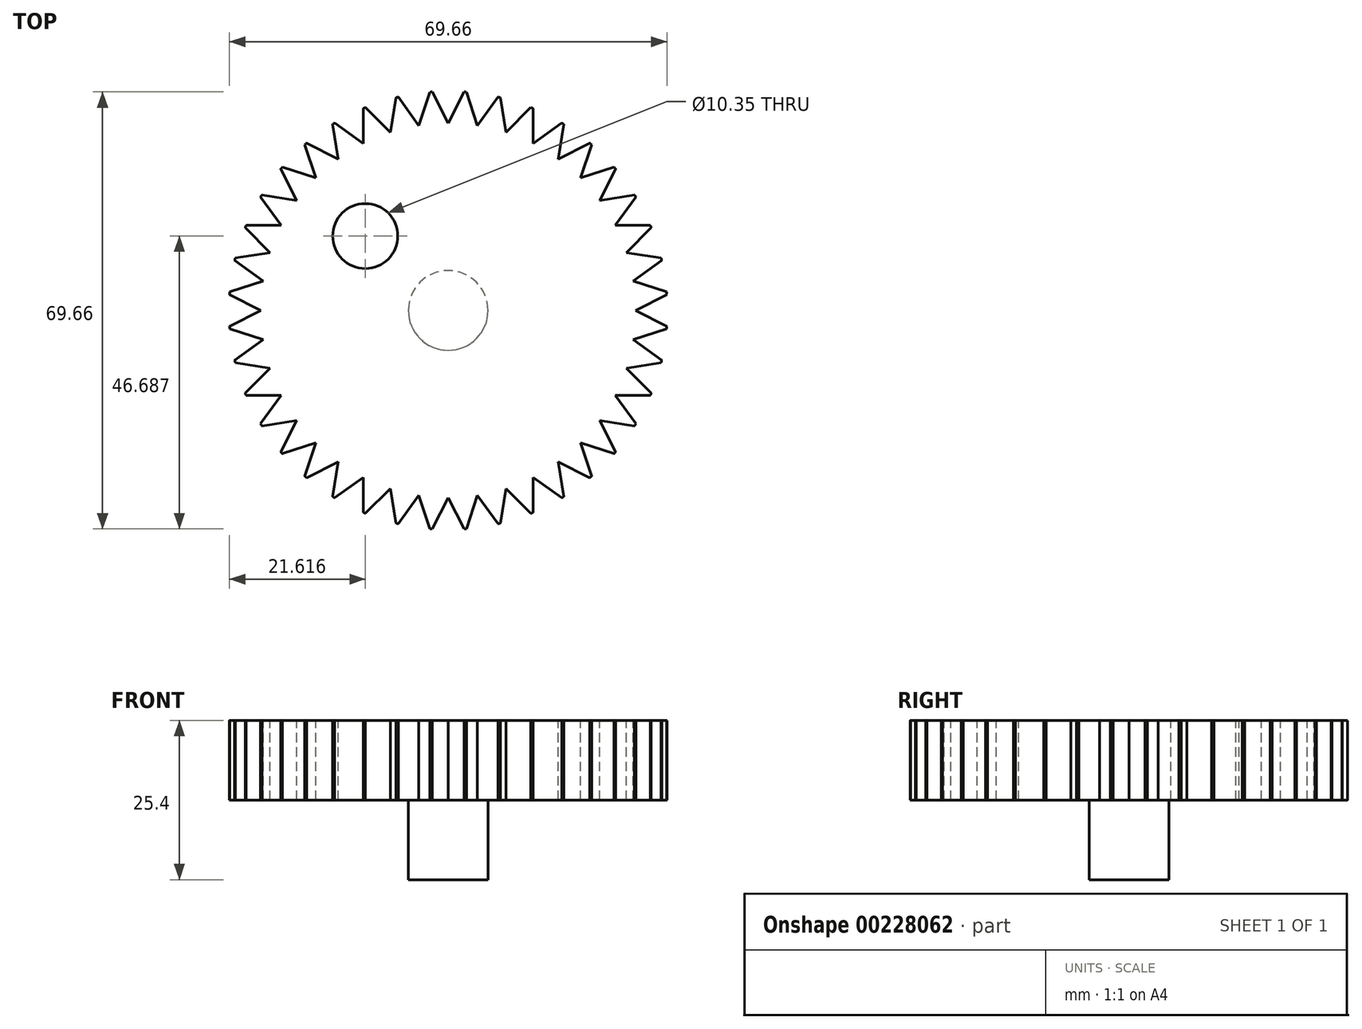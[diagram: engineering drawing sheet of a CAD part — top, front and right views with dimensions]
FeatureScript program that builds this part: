
annotation { "Feature Type Name" : "Feature", "Feature Type Description" : "" }
export const myFeature = defineFeature(function(context is Context, id is Id, definition is map)
    precondition{}
    {
        {
            var Q0;
            Q0=qCreatedBy(makeId("Top.planeOp"),FACE);
            var sketch = newSketch(context, id + "F0", { "sketchPlane" : qUnion([Q0])});
            skCircle(sketch, "E0", {"center": v(0, 0) * mm, "radius": 19.05 * mm});
            skSolve(sketch);
        }
        {
            var Q0;
            Q0=qSketchRegion(id+"F0",true);
            extrude(context, id + "F1", {"entities" : qUnion([Q0]), "depth" : 6.35 * mm, "offsetDistance" : 25.4 * mm});
        }
        {
            var Q0;
            Q0=makeQuery(id+"F1.opExtrude","CAP_FACE",FACE,{"disambiguationData":[OSD([sQuery(id+"F0.wireOp",EDGE,"E0")])],"isStart":false});
            var sketch = newSketch(context, id + "F2", { "sketchPlane" : qUnion([Q0])});
            skCircle(sketch, "E1", {"center": v(0, 0) * mm, "radius": 6.35 * mm});
            skSolve(sketch);
        }
        {
            var Q0;
            Q0=qSketchRegion(id+"F2",true);
            extrude(context, id + "F3", {"entities" : qUnion([Q0]), "operationType" : NewBodyOperationType.ADD, "depth" : 31.75 * mm, "offsetDistance" : 25.4 * mm});
        }
        {
            var Q0;
            Q0=makeQuery(id+"F3.opExtrude","CAP_FACE",FACE,{"disambiguationData":[OSD([sQuery(id+"F2.wireOp",EDGE,"E1")])],"isStart":false});
            var sketch = newSketch(context, id + "F4", { "sketchPlane" : qUnion([Q0])});
            skCircle(sketch, "E2", {"center": v(0, 0) * mm, "radius": 34.93 * mm});
            skSolve(sketch);
        }
        {
            var Q0;
            Q0=qSketchRegion(id+"F4",true);
            extrude(context, id + "F5", {"entities" : qUnion([Q0]), "operationType" : NewBodyOperationType.ADD, "depth" : 12.7 * mm, "offsetDistance" : 25.4 * mm});
        }
        {
            var Q0;
            Q0=makeQuery(id+"F1.opExtrude","CAP_FACE",FACE,{"disambiguationData":[OSD([sQuery(id+"F0.wireOp",EDGE,"E0")])],"isStart":true});
            var sketch = newSketch(context, id + "F6", { "sketchPlane" : qUnion([Q0])});
            skLineSegment(sketch, "E3", {"start": v(0, 16.51) * mm, "end": v(2.54, 18.88) * mm});
            skLineSegment(sketch, "E4", {"start": v(0, 16.51) * mm, "end": v(0, 19.05) * mm, "construction": true});
            skLineSegment(sketch, "E5", {"start": v(0, 16.51) * mm, "end": v(-2.54, 18.88) * mm});
            skArc(sketch, "E6", {"start": v(2.54, 18.88) * mm, "mid": v(0, 19.05) * mm, "end": v(-2.54, 18.88) * mm});
            skLineSegment(sketch, "E7.1.0", {"start": v(-5.1, 15.7) * mm, "end": v(-5.89, 18.12) * mm, "construction": true});
            skLineSegment(sketch, "E7.1.1", {"start": v(-5.1, 15.7) * mm, "end": v(-8.25, 17.17) * mm});
            skArc(sketch, "E7.1.2", {"start": v(-3.42, 18.74) * mm, "mid": v(-5.89, 18.12) * mm, "end": v(-8.25, 17.17) * mm});
            skLineSegment(sketch, "E7.1.3", {"start": v(-5.1, 15.7) * mm, "end": v(-3.42, 18.74) * mm});
            skLineSegment(sketch, "E7.2.0", {"start": v(-9.7, 13.36) * mm, "end": v(-11.2, 15.41) * mm, "construction": true});
            skLineSegment(sketch, "E7.2.1", {"start": v(-9.7, 13.36) * mm, "end": v(-13.15, 13.78) * mm});
            skArc(sketch, "E7.2.2", {"start": v(-9.04, 16.77) * mm, "mid": v(-11.2, 15.41) * mm, "end": v(-13.15, 13.78) * mm});
            skLineSegment(sketch, "E7.2.3", {"start": v(-9.7, 13.36) * mm, "end": v(-9.04, 16.77) * mm});
            skLineSegment(sketch, "E7.3.0", {"start": v(-13.36, 9.7) * mm, "end": v(-15.41, 11.2) * mm, "construction": true});
            skLineSegment(sketch, "E7.3.1", {"start": v(-13.36, 9.7) * mm, "end": v(-16.77, 9.04) * mm});
            skArc(sketch, "E7.3.2", {"start": v(-13.78, 13.15) * mm, "mid": v(-15.41, 11.2) * mm, "end": v(-16.77, 9.04) * mm});
            skLineSegment(sketch, "E7.3.3", {"start": v(-13.36, 9.7) * mm, "end": v(-13.78, 13.15) * mm});
            skLineSegment(sketch, "E7.4.0", {"start": v(-15.7, 5.1) * mm, "end": v(-18.12, 5.89) * mm, "construction": true});
            skLineSegment(sketch, "E7.4.1", {"start": v(-15.7, 5.1) * mm, "end": v(-18.74, 3.42) * mm});
            skArc(sketch, "E7.4.2", {"start": v(-17.17, 8.25) * mm, "mid": v(-18.12, 5.89) * mm, "end": v(-18.74, 3.42) * mm});
            skLineSegment(sketch, "E7.4.3", {"start": v(-15.7, 5.1) * mm, "end": v(-17.17, 8.25) * mm});
            skLineSegment(sketch, "E7.5.0", {"start": v(-16.51, 0) * mm, "end": v(-19.05, 0) * mm, "construction": true});
            skLineSegment(sketch, "E7.5.1", {"start": v(-16.51, 0) * mm, "end": v(-18.88, -2.54) * mm});
            skArc(sketch, "E7.5.2", {"start": v(-18.88, 2.54) * mm, "mid": v(-19.05, 0) * mm, "end": v(-18.88, -2.54) * mm});
            skLineSegment(sketch, "E7.5.3", {"start": v(-16.51, 0) * mm, "end": v(-18.88, 2.54) * mm});
            skLineSegment(sketch, "E7.6.0", {"start": v(-15.7, -5.1) * mm, "end": v(-18.12, -5.89) * mm, "construction": true});
            skLineSegment(sketch, "E7.6.1", {"start": v(-15.7, -5.1) * mm, "end": v(-17.17, -8.25) * mm});
            skArc(sketch, "E7.6.2", {"start": v(-18.74, -3.42) * mm, "mid": v(-18.12, -5.89) * mm, "end": v(-17.17, -8.25) * mm});
            skLineSegment(sketch, "E7.6.3", {"start": v(-15.7, -5.1) * mm, "end": v(-18.74, -3.42) * mm});
            skLineSegment(sketch, "E7.7.0", {"start": v(-13.36, -9.7) * mm, "end": v(-15.41, -11.2) * mm, "construction": true});
            skLineSegment(sketch, "E7.7.1", {"start": v(-13.36, -9.7) * mm, "end": v(-13.78, -13.15) * mm});
            skArc(sketch, "E7.7.2", {"start": v(-16.77, -9.04) * mm, "mid": v(-15.41, -11.2) * mm, "end": v(-13.78, -13.15) * mm});
            skLineSegment(sketch, "E7.7.3", {"start": v(-13.36, -9.7) * mm, "end": v(-16.77, -9.04) * mm});
            skLineSegment(sketch, "E7.8.0", {"start": v(-9.7, -13.36) * mm, "end": v(-11.2, -15.41) * mm, "construction": true});
            skLineSegment(sketch, "E7.8.1", {"start": v(-9.7, -13.36) * mm, "end": v(-9.04, -16.77) * mm});
            skArc(sketch, "E7.8.2", {"start": v(-13.15, -13.78) * mm, "mid": v(-11.2, -15.41) * mm, "end": v(-9.04, -16.77) * mm});
            skLineSegment(sketch, "E7.8.3", {"start": v(-9.7, -13.36) * mm, "end": v(-13.15, -13.78) * mm});
            skLineSegment(sketch, "E7.9.0", {"start": v(-5.1, -15.7) * mm, "end": v(-5.89, -18.12) * mm, "construction": true});
            skLineSegment(sketch, "E7.9.1", {"start": v(-5.1, -15.7) * mm, "end": v(-3.42, -18.74) * mm});
            skArc(sketch, "E7.9.2", {"start": v(-8.25, -17.17) * mm, "mid": v(-5.89, -18.12) * mm, "end": v(-3.42, -18.74) * mm});
            skLineSegment(sketch, "E7.9.3", {"start": v(-5.1, -15.7) * mm, "end": v(-8.25, -17.17) * mm});
            skLineSegment(sketch, "E7.10.0", {"start": v(0, -16.51) * mm, "end": v(0, -19.05) * mm, "construction": true});
            skLineSegment(sketch, "E7.10.1", {"start": v(0, -16.51) * mm, "end": v(2.54, -18.88) * mm});
            skArc(sketch, "E7.10.2", {"start": v(-2.54, -18.88) * mm, "mid": v(0, -19.05) * mm, "end": v(2.54, -18.88) * mm});
            skLineSegment(sketch, "E7.10.3", {"start": v(0, -16.51) * mm, "end": v(-2.54, -18.88) * mm});
            skLineSegment(sketch, "E7.11.0", {"start": v(5.1, -15.7) * mm, "end": v(5.89, -18.12) * mm, "construction": true});
            skLineSegment(sketch, "E7.11.1", {"start": v(5.1, -15.7) * mm, "end": v(8.25, -17.17) * mm});
            skArc(sketch, "E7.11.2", {"start": v(3.42, -18.74) * mm, "mid": v(5.89, -18.12) * mm, "end": v(8.25, -17.17) * mm});
            skLineSegment(sketch, "E7.11.3", {"start": v(5.1, -15.7) * mm, "end": v(3.42, -18.74) * mm});
            skLineSegment(sketch, "E7.12.0", {"start": v(9.7, -13.36) * mm, "end": v(11.2, -15.41) * mm, "construction": true});
            skLineSegment(sketch, "E7.12.1", {"start": v(9.7, -13.36) * mm, "end": v(13.15, -13.78) * mm});
            skArc(sketch, "E7.12.2", {"start": v(9.04, -16.77) * mm, "mid": v(11.2, -15.41) * mm, "end": v(13.15, -13.78) * mm});
            skLineSegment(sketch, "E7.12.3", {"start": v(9.7, -13.36) * mm, "end": v(9.04, -16.77) * mm});
            skLineSegment(sketch, "E7.13.0", {"start": v(13.36, -9.7) * mm, "end": v(15.41, -11.2) * mm, "construction": true});
            skLineSegment(sketch, "E7.13.1", {"start": v(13.36, -9.7) * mm, "end": v(16.77, -9.04) * mm});
            skArc(sketch, "E7.13.2", {"start": v(13.78, -13.15) * mm, "mid": v(15.41, -11.2) * mm, "end": v(16.77, -9.04) * mm});
            skLineSegment(sketch, "E7.13.3", {"start": v(13.36, -9.7) * mm, "end": v(13.78, -13.15) * mm});
            skLineSegment(sketch, "E7.14.0", {"start": v(15.7, -5.1) * mm, "end": v(18.12, -5.89) * mm, "construction": true});
            skLineSegment(sketch, "E7.14.1", {"start": v(15.7, -5.1) * mm, "end": v(18.74, -3.42) * mm});
            skArc(sketch, "E7.14.2", {"start": v(17.17, -8.25) * mm, "mid": v(18.12, -5.89) * mm, "end": v(18.74, -3.42) * mm});
            skLineSegment(sketch, "E7.14.3", {"start": v(15.7, -5.1) * mm, "end": v(17.17, -8.25) * mm});
            skLineSegment(sketch, "E7.15.0", {"start": v(16.51, 0) * mm, "end": v(19.05, 0) * mm, "construction": true});
            skLineSegment(sketch, "E7.15.1", {"start": v(16.51, 0) * mm, "end": v(18.88, 2.54) * mm});
            skArc(sketch, "E7.15.2", {"start": v(18.88, -2.54) * mm, "mid": v(19.05, 0) * mm, "end": v(18.88, 2.54) * mm});
            skLineSegment(sketch, "E7.15.3", {"start": v(16.51, 0) * mm, "end": v(18.88, -2.54) * mm});
            skLineSegment(sketch, "E7.16.0", {"start": v(15.7, 5.1) * mm, "end": v(18.12, 5.89) * mm, "construction": true});
            skLineSegment(sketch, "E7.16.1", {"start": v(15.7, 5.1) * mm, "end": v(17.17, 8.25) * mm});
            skArc(sketch, "E7.16.2", {"start": v(18.74, 3.42) * mm, "mid": v(18.12, 5.89) * mm, "end": v(17.17, 8.25) * mm});
            skLineSegment(sketch, "E7.16.3", {"start": v(15.7, 5.1) * mm, "end": v(18.74, 3.42) * mm});
            skLineSegment(sketch, "E7.17.0", {"start": v(13.36, 9.7) * mm, "end": v(15.41, 11.2) * mm, "construction": true});
            skLineSegment(sketch, "E7.17.1", {"start": v(13.36, 9.7) * mm, "end": v(13.78, 13.15) * mm});
            skArc(sketch, "E7.17.2", {"start": v(16.77, 9.04) * mm, "mid": v(15.41, 11.2) * mm, "end": v(13.78, 13.15) * mm});
            skLineSegment(sketch, "E7.17.3", {"start": v(13.36, 9.7) * mm, "end": v(16.77, 9.04) * mm});
            skLineSegment(sketch, "E7.18.0", {"start": v(9.7, 13.36) * mm, "end": v(11.2, 15.41) * mm, "construction": true});
            skLineSegment(sketch, "E7.18.1", {"start": v(9.7, 13.36) * mm, "end": v(9.04, 16.77) * mm});
            skArc(sketch, "E7.18.2", {"start": v(13.15, 13.78) * mm, "mid": v(11.2, 15.41) * mm, "end": v(9.04, 16.77) * mm});
            skLineSegment(sketch, "E7.18.3", {"start": v(9.7, 13.36) * mm, "end": v(13.15, 13.78) * mm});
            skLineSegment(sketch, "E7.19.0", {"start": v(5.1, 15.7) * mm, "end": v(5.89, 18.12) * mm, "construction": true});
            skLineSegment(sketch, "E7.19.1", {"start": v(5.1, 15.7) * mm, "end": v(3.42, 18.74) * mm});
            skArc(sketch, "E7.19.2", {"start": v(8.25, 17.17) * mm, "mid": v(5.89, 18.12) * mm, "end": v(3.42, 18.74) * mm});
            skLineSegment(sketch, "E7.19.3", {"start": v(5.1, 15.7) * mm, "end": v(8.25, 17.17) * mm});
            skSolve(sketch);
        }
        {
            var Q0;
            Q0=qSketchRegion(id+"F6",true);
            extrude(context, id + "F7", {"entities" : qUnion([Q0]), "operationType" : NewBodyOperationType.REMOVE, "oppositeDirection" : true, "depth" : 25.4 * mm, "offsetDistance" : 25.4 * mm});
        }
        {
            var Q0;
            Q0=makeQuery(id+"F5.opExtrude","CAP_FACE",FACE,{"disambiguationData":[OSD([sQuery(id+"F4.wireOp",EDGE,"E2")])],"isStart":false});
            var sketch = newSketch(context, id + "F8", { "sketchPlane" : qUnion([Q0])});
            skLineSegment(sketch, "E8", {"start": v(0, 34.93) * mm, "end": v(0, 29.85) * mm, "construction": true});
            skLineSegment(sketch, "E9", {"start": v(0, 29.85) * mm, "end": v(2.54, 34.83) * mm});
            skLineSegment(sketch, "E10", {"start": v(0, 29.85) * mm, "end": v(-2.54, 34.83) * mm});
            skArc(sketch, "E11", {"start": v(2.54, 34.83) * mm, "mid": v(0, 34.93) * mm, "end": v(-2.54, 34.83) * mm});
            skLineSegment(sketch, "E12.1.0", {"start": v(-4.67, 29.48) * mm, "end": v(-2.94, 34.8) * mm});
            skLineSegment(sketch, "E12.1.1", {"start": v(-4.67, 29.48) * mm, "end": v(-7.96, 34) * mm});
            skLineSegment(sketch, "E12.1.2", {"start": v(-5.46, 34.5) * mm, "end": v(-4.67, 29.48) * mm, "construction": true});
            skArc(sketch, "E12.1.3", {"start": v(-2.94, 34.8) * mm, "mid": v(-5.46, 34.5) * mm, "end": v(-7.96, 34) * mm});
            skLineSegment(sketch, "E12.2.0", {"start": v(-9.22, 28.38) * mm, "end": v(-8.35, 33.91) * mm});
            skLineSegment(sketch, "E12.2.1", {"start": v(-9.22, 28.38) * mm, "end": v(-13.18, 32.34) * mm});
            skLineSegment(sketch, "E12.2.2", {"start": v(-10.8, 33.22) * mm, "end": v(-9.22, 28.38) * mm, "construction": true});
            skArc(sketch, "E12.2.3", {"start": v(-8.35, 33.91) * mm, "mid": v(-10.8, 33.22) * mm, "end": v(-13.18, 32.34) * mm});
            skLineSegment(sketch, "E12.3.0", {"start": v(-13.55, 26.6) * mm, "end": v(-13.55, 32.19) * mm});
            skLineSegment(sketch, "E12.3.1", {"start": v(-13.55, 26.6) * mm, "end": v(-18.08, 29.88) * mm});
            skLineSegment(sketch, "E12.3.2", {"start": v(-15.86, 31.12) * mm, "end": v(-13.55, 26.6) * mm, "construction": true});
            skArc(sketch, "E12.3.3", {"start": v(-13.55, 32.19) * mm, "mid": v(-15.86, 31.12) * mm, "end": v(-18.08, 29.88) * mm});
            skLineSegment(sketch, "E12.4.0", {"start": v(-17.54, 24.15) * mm, "end": v(-18.42, 29.67) * mm});
            skLineSegment(sketch, "E12.4.1", {"start": v(-17.54, 24.15) * mm, "end": v(-22.53, 26.69) * mm});
            skLineSegment(sketch, "E12.4.2", {"start": v(-20.53, 28.25) * mm, "end": v(-17.54, 24.15) * mm, "construction": true});
            skArc(sketch, "E12.4.3", {"start": v(-18.42, 29.67) * mm, "mid": v(-20.53, 28.25) * mm, "end": v(-22.53, 26.69) * mm});
            skLineSegment(sketch, "E12.5.0", {"start": v(-21.1, 21.1) * mm, "end": v(-22.83, 26.43) * mm});
            skLineSegment(sketch, "E12.5.1", {"start": v(-21.1, 21.1) * mm, "end": v(-26.43, 22.83) * mm});
            skLineSegment(sketch, "E12.5.2", {"start": v(-24.7, 24.7) * mm, "end": v(-21.1, 21.1) * mm, "construction": true});
            skArc(sketch, "E12.5.3", {"start": v(-22.83, 26.43) * mm, "mid": v(-24.7, 24.7) * mm, "end": v(-26.43, 22.83) * mm});
            skLineSegment(sketch, "E12.6.0", {"start": v(-24.15, 17.54) * mm, "end": v(-26.69, 22.53) * mm});
            skLineSegment(sketch, "E12.6.1", {"start": v(-24.15, 17.54) * mm, "end": v(-29.67, 18.42) * mm});
            skLineSegment(sketch, "E12.6.2", {"start": v(-28.25, 20.53) * mm, "end": v(-24.15, 17.54) * mm, "construction": true});
            skArc(sketch, "E12.6.3", {"start": v(-26.69, 22.53) * mm, "mid": v(-28.25, 20.53) * mm, "end": v(-29.67, 18.42) * mm});
            skLineSegment(sketch, "E12.7.0", {"start": v(-26.6, 13.55) * mm, "end": v(-29.88, 18.08) * mm});
            skLineSegment(sketch, "E12.7.1", {"start": v(-26.6, 13.55) * mm, "end": v(-32.19, 13.55) * mm});
            skLineSegment(sketch, "E12.7.2", {"start": v(-31.12, 15.86) * mm, "end": v(-26.6, 13.55) * mm, "construction": true});
            skArc(sketch, "E12.7.3", {"start": v(-29.88, 18.08) * mm, "mid": v(-31.12, 15.86) * mm, "end": v(-32.19, 13.55) * mm});
            skLineSegment(sketch, "E12.8.0", {"start": v(-28.38, 9.22) * mm, "end": v(-32.34, 13.18) * mm});
            skLineSegment(sketch, "E12.8.1", {"start": v(-28.38, 9.22) * mm, "end": v(-33.91, 8.35) * mm});
            skLineSegment(sketch, "E12.8.2", {"start": v(-33.22, 10.8) * mm, "end": v(-28.38, 9.22) * mm, "construction": true});
            skArc(sketch, "E12.8.3", {"start": v(-32.34, 13.18) * mm, "mid": v(-33.22, 10.8) * mm, "end": v(-33.91, 8.35) * mm});
            skLineSegment(sketch, "E12.9.0", {"start": v(-29.48, 4.67) * mm, "end": v(-34, 7.96) * mm});
            skLineSegment(sketch, "E12.9.1", {"start": v(-29.48, 4.67) * mm, "end": v(-34.8, 2.94) * mm});
            skLineSegment(sketch, "E12.9.2", {"start": v(-34.5, 5.46) * mm, "end": v(-29.48, 4.67) * mm, "construction": true});
            skArc(sketch, "E12.9.3", {"start": v(-34, 7.96) * mm, "mid": v(-34.5, 5.46) * mm, "end": v(-34.8, 2.94) * mm});
            skLineSegment(sketch, "E12.10.0", {"start": v(-29.85, 0) * mm, "end": v(-34.83, 2.54) * mm});
            skLineSegment(sketch, "E12.10.1", {"start": v(-29.85, 0) * mm, "end": v(-34.83, -2.54) * mm});
            skLineSegment(sketch, "E12.10.2", {"start": v(-34.93, 0) * mm, "end": v(-29.85, 0) * mm, "construction": true});
            skArc(sketch, "E12.10.3", {"start": v(-34.83, 2.54) * mm, "mid": v(-34.93, 0) * mm, "end": v(-34.83, -2.54) * mm});
            skLineSegment(sketch, "E12.11.0", {"start": v(-29.48, -4.67) * mm, "end": v(-34.8, -2.94) * mm});
            skLineSegment(sketch, "E12.11.1", {"start": v(-29.48, -4.67) * mm, "end": v(-34, -7.96) * mm});
            skLineSegment(sketch, "E12.11.2", {"start": v(-34.5, -5.46) * mm, "end": v(-29.48, -4.67) * mm, "construction": true});
            skArc(sketch, "E12.11.3", {"start": v(-34.8, -2.94) * mm, "mid": v(-34.5, -5.46) * mm, "end": v(-34, -7.96) * mm});
            skLineSegment(sketch, "E12.12.0", {"start": v(-28.38, -9.22) * mm, "end": v(-33.91, -8.35) * mm});
            skLineSegment(sketch, "E12.12.1", {"start": v(-28.38, -9.22) * mm, "end": v(-32.34, -13.18) * mm});
            skLineSegment(sketch, "E12.12.2", {"start": v(-33.22, -10.8) * mm, "end": v(-28.38, -9.22) * mm, "construction": true});
            skArc(sketch, "E12.12.3", {"start": v(-33.91, -8.35) * mm, "mid": v(-33.22, -10.8) * mm, "end": v(-32.34, -13.18) * mm});
            skLineSegment(sketch, "E12.13.0", {"start": v(-26.6, -13.55) * mm, "end": v(-32.19, -13.55) * mm});
            skLineSegment(sketch, "E12.13.1", {"start": v(-26.6, -13.55) * mm, "end": v(-29.88, -18.08) * mm});
            skLineSegment(sketch, "E12.13.2", {"start": v(-31.12, -15.86) * mm, "end": v(-26.6, -13.55) * mm, "construction": true});
            skArc(sketch, "E12.13.3", {"start": v(-32.19, -13.55) * mm, "mid": v(-31.12, -15.86) * mm, "end": v(-29.88, -18.08) * mm});
            skLineSegment(sketch, "E12.14.0", {"start": v(-24.15, -17.54) * mm, "end": v(-29.67, -18.42) * mm});
            skLineSegment(sketch, "E12.14.1", {"start": v(-24.15, -17.54) * mm, "end": v(-26.69, -22.53) * mm});
            skLineSegment(sketch, "E12.14.2", {"start": v(-28.25, -20.53) * mm, "end": v(-24.15, -17.54) * mm, "construction": true});
            skArc(sketch, "E12.14.3", {"start": v(-29.67, -18.42) * mm, "mid": v(-28.25, -20.53) * mm, "end": v(-26.69, -22.53) * mm});
            skLineSegment(sketch, "E12.15.0", {"start": v(-21.1, -21.1) * mm, "end": v(-26.43, -22.83) * mm});
            skLineSegment(sketch, "E12.15.1", {"start": v(-21.1, -21.1) * mm, "end": v(-22.83, -26.43) * mm});
            skLineSegment(sketch, "E12.15.2", {"start": v(-24.7, -24.7) * mm, "end": v(-21.1, -21.1) * mm, "construction": true});
            skArc(sketch, "E12.15.3", {"start": v(-26.43, -22.83) * mm, "mid": v(-24.7, -24.7) * mm, "end": v(-22.83, -26.43) * mm});
            skLineSegment(sketch, "E12.16.0", {"start": v(-17.54, -24.15) * mm, "end": v(-22.53, -26.69) * mm});
            skLineSegment(sketch, "E12.16.1", {"start": v(-17.54, -24.15) * mm, "end": v(-18.42, -29.67) * mm});
            skLineSegment(sketch, "E12.16.2", {"start": v(-20.53, -28.25) * mm, "end": v(-17.54, -24.15) * mm, "construction": true});
            skArc(sketch, "E12.16.3", {"start": v(-22.53, -26.69) * mm, "mid": v(-20.53, -28.25) * mm, "end": v(-18.42, -29.67) * mm});
            skLineSegment(sketch, "E12.17.0", {"start": v(-13.55, -26.6) * mm, "end": v(-18.08, -29.88) * mm});
            skLineSegment(sketch, "E12.17.1", {"start": v(-13.55, -26.6) * mm, "end": v(-13.55, -32.19) * mm});
            skLineSegment(sketch, "E12.17.2", {"start": v(-15.86, -31.12) * mm, "end": v(-13.55, -26.6) * mm, "construction": true});
            skArc(sketch, "E12.17.3", {"start": v(-18.08, -29.88) * mm, "mid": v(-15.86, -31.12) * mm, "end": v(-13.55, -32.19) * mm});
            skLineSegment(sketch, "E12.18.0", {"start": v(-9.22, -28.38) * mm, "end": v(-13.18, -32.34) * mm});
            skLineSegment(sketch, "E12.18.1", {"start": v(-9.22, -28.38) * mm, "end": v(-8.35, -33.91) * mm});
            skLineSegment(sketch, "E12.18.2", {"start": v(-10.8, -33.22) * mm, "end": v(-9.22, -28.38) * mm, "construction": true});
            skArc(sketch, "E12.18.3", {"start": v(-13.18, -32.34) * mm, "mid": v(-10.8, -33.22) * mm, "end": v(-8.35, -33.91) * mm});
            skLineSegment(sketch, "E12.19.0", {"start": v(-4.67, -29.48) * mm, "end": v(-7.96, -34) * mm});
            skLineSegment(sketch, "E12.19.1", {"start": v(-4.67, -29.48) * mm, "end": v(-2.94, -34.8) * mm});
            skLineSegment(sketch, "E12.19.2", {"start": v(-5.46, -34.5) * mm, "end": v(-4.67, -29.48) * mm, "construction": true});
            skArc(sketch, "E12.19.3", {"start": v(-7.96, -34) * mm, "mid": v(-5.46, -34.5) * mm, "end": v(-2.94, -34.8) * mm});
            skLineSegment(sketch, "E12.20.0", {"start": v(0, -29.85) * mm, "end": v(-2.54, -34.83) * mm});
            skLineSegment(sketch, "E12.20.1", {"start": v(0, -29.85) * mm, "end": v(2.54, -34.83) * mm});
            skLineSegment(sketch, "E12.20.2", {"start": v(0, -34.93) * mm, "end": v(0, -29.85) * mm, "construction": true});
            skArc(sketch, "E12.20.3", {"start": v(-2.54, -34.83) * mm, "mid": v(0, -34.93) * mm, "end": v(2.54, -34.83) * mm});
            skLineSegment(sketch, "E12.21.0", {"start": v(4.67, -29.48) * mm, "end": v(2.94, -34.8) * mm});
            skLineSegment(sketch, "E12.21.1", {"start": v(4.67, -29.48) * mm, "end": v(7.96, -34) * mm});
            skLineSegment(sketch, "E12.21.2", {"start": v(5.46, -34.5) * mm, "end": v(4.67, -29.48) * mm, "construction": true});
            skArc(sketch, "E12.21.3", {"start": v(2.94, -34.8) * mm, "mid": v(5.46, -34.5) * mm, "end": v(7.96, -34) * mm});
            skLineSegment(sketch, "E12.22.0", {"start": v(9.22, -28.38) * mm, "end": v(8.35, -33.91) * mm});
            skLineSegment(sketch, "E12.22.1", {"start": v(9.22, -28.38) * mm, "end": v(13.18, -32.34) * mm});
            skLineSegment(sketch, "E12.22.2", {"start": v(10.8, -33.22) * mm, "end": v(9.22, -28.38) * mm, "construction": true});
            skArc(sketch, "E12.22.3", {"start": v(8.35, -33.91) * mm, "mid": v(10.8, -33.22) * mm, "end": v(13.18, -32.34) * mm});
            skLineSegment(sketch, "E12.23.0", {"start": v(13.55, -26.6) * mm, "end": v(13.55, -32.19) * mm});
            skLineSegment(sketch, "E12.23.1", {"start": v(13.55, -26.6) * mm, "end": v(18.08, -29.88) * mm});
            skLineSegment(sketch, "E12.23.2", {"start": v(15.86, -31.12) * mm, "end": v(13.55, -26.6) * mm, "construction": true});
            skArc(sketch, "E12.23.3", {"start": v(13.55, -32.19) * mm, "mid": v(15.86, -31.12) * mm, "end": v(18.08, -29.88) * mm});
            skLineSegment(sketch, "E12.24.0", {"start": v(17.54, -24.15) * mm, "end": v(18.42, -29.67) * mm});
            skLineSegment(sketch, "E12.24.1", {"start": v(17.54, -24.15) * mm, "end": v(22.53, -26.69) * mm});
            skLineSegment(sketch, "E12.24.2", {"start": v(20.53, -28.25) * mm, "end": v(17.54, -24.15) * mm, "construction": true});
            skArc(sketch, "E12.24.3", {"start": v(18.42, -29.67) * mm, "mid": v(20.53, -28.25) * mm, "end": v(22.53, -26.69) * mm});
            skLineSegment(sketch, "E12.25.0", {"start": v(21.1, -21.1) * mm, "end": v(22.83, -26.43) * mm});
            skLineSegment(sketch, "E12.25.1", {"start": v(21.1, -21.1) * mm, "end": v(26.43, -22.83) * mm});
            skLineSegment(sketch, "E12.25.2", {"start": v(24.7, -24.7) * mm, "end": v(21.1, -21.1) * mm, "construction": true});
            skArc(sketch, "E12.25.3", {"start": v(22.83, -26.43) * mm, "mid": v(24.7, -24.7) * mm, "end": v(26.43, -22.83) * mm});
            skLineSegment(sketch, "E12.26.0", {"start": v(24.15, -17.54) * mm, "end": v(26.69, -22.53) * mm});
            skLineSegment(sketch, "E12.26.1", {"start": v(24.15, -17.54) * mm, "end": v(29.67, -18.42) * mm});
            skLineSegment(sketch, "E12.26.2", {"start": v(28.25, -20.53) * mm, "end": v(24.15, -17.54) * mm, "construction": true});
            skArc(sketch, "E12.26.3", {"start": v(26.69, -22.53) * mm, "mid": v(28.25, -20.53) * mm, "end": v(29.67, -18.42) * mm});
            skLineSegment(sketch, "E12.27.0", {"start": v(26.6, -13.55) * mm, "end": v(29.88, -18.08) * mm});
            skLineSegment(sketch, "E12.27.1", {"start": v(26.6, -13.55) * mm, "end": v(32.19, -13.55) * mm});
            skLineSegment(sketch, "E12.27.2", {"start": v(31.12, -15.86) * mm, "end": v(26.6, -13.55) * mm, "construction": true});
            skArc(sketch, "E12.27.3", {"start": v(29.88, -18.08) * mm, "mid": v(31.12, -15.86) * mm, "end": v(32.19, -13.55) * mm});
            skLineSegment(sketch, "E12.28.0", {"start": v(28.38, -9.22) * mm, "end": v(32.34, -13.18) * mm});
            skLineSegment(sketch, "E12.28.1", {"start": v(28.38, -9.22) * mm, "end": v(33.91, -8.35) * mm});
            skLineSegment(sketch, "E12.28.2", {"start": v(33.22, -10.8) * mm, "end": v(28.38, -9.22) * mm, "construction": true});
            skArc(sketch, "E12.28.3", {"start": v(32.34, -13.18) * mm, "mid": v(33.22, -10.8) * mm, "end": v(33.91, -8.35) * mm});
            skLineSegment(sketch, "E12.29.0", {"start": v(29.48, -4.67) * mm, "end": v(34, -7.96) * mm});
            skLineSegment(sketch, "E12.29.1", {"start": v(29.48, -4.67) * mm, "end": v(34.8, -2.94) * mm});
            skLineSegment(sketch, "E12.29.2", {"start": v(34.5, -5.46) * mm, "end": v(29.48, -4.67) * mm, "construction": true});
            skArc(sketch, "E12.29.3", {"start": v(34, -7.96) * mm, "mid": v(34.5, -5.46) * mm, "end": v(34.8, -2.94) * mm});
            skLineSegment(sketch, "E12.30.0", {"start": v(29.85, 0) * mm, "end": v(34.83, -2.54) * mm});
            skLineSegment(sketch, "E12.30.1", {"start": v(29.85, 0) * mm, "end": v(34.83, 2.54) * mm});
            skLineSegment(sketch, "E12.30.2", {"start": v(34.93, 0) * mm, "end": v(29.85, 0) * mm, "construction": true});
            skArc(sketch, "E12.30.3", {"start": v(34.83, -2.54) * mm, "mid": v(34.93, 0) * mm, "end": v(34.83, 2.54) * mm});
            skLineSegment(sketch, "E12.31.0", {"start": v(29.48, 4.67) * mm, "end": v(34.8, 2.94) * mm});
            skLineSegment(sketch, "E12.31.1", {"start": v(29.48, 4.67) * mm, "end": v(34, 7.96) * mm});
            skLineSegment(sketch, "E12.31.2", {"start": v(34.5, 5.46) * mm, "end": v(29.48, 4.67) * mm, "construction": true});
            skArc(sketch, "E12.31.3", {"start": v(34.8, 2.94) * mm, "mid": v(34.5, 5.46) * mm, "end": v(34, 7.96) * mm});
            skLineSegment(sketch, "E12.32.0", {"start": v(28.38, 9.22) * mm, "end": v(33.91, 8.35) * mm});
            skLineSegment(sketch, "E12.32.1", {"start": v(28.38, 9.22) * mm, "end": v(32.34, 13.18) * mm});
            skLineSegment(sketch, "E12.32.2", {"start": v(33.22, 10.8) * mm, "end": v(28.38, 9.22) * mm, "construction": true});
            skArc(sketch, "E12.32.3", {"start": v(33.91, 8.35) * mm, "mid": v(33.22, 10.8) * mm, "end": v(32.34, 13.18) * mm});
            skLineSegment(sketch, "E12.33.0", {"start": v(26.6, 13.55) * mm, "end": v(32.19, 13.55) * mm});
            skLineSegment(sketch, "E12.33.1", {"start": v(26.6, 13.55) * mm, "end": v(29.88, 18.08) * mm});
            skLineSegment(sketch, "E12.33.2", {"start": v(31.12, 15.86) * mm, "end": v(26.6, 13.55) * mm, "construction": true});
            skArc(sketch, "E12.33.3", {"start": v(32.19, 13.55) * mm, "mid": v(31.12, 15.86) * mm, "end": v(29.88, 18.08) * mm});
            skLineSegment(sketch, "E12.34.0", {"start": v(24.15, 17.54) * mm, "end": v(29.67, 18.42) * mm});
            skLineSegment(sketch, "E12.34.1", {"start": v(24.15, 17.54) * mm, "end": v(26.69, 22.53) * mm});
            skLineSegment(sketch, "E12.34.2", {"start": v(28.25, 20.53) * mm, "end": v(24.15, 17.54) * mm, "construction": true});
            skArc(sketch, "E12.34.3", {"start": v(29.67, 18.42) * mm, "mid": v(28.25, 20.53) * mm, "end": v(26.69, 22.53) * mm});
            skLineSegment(sketch, "E12.35.0", {"start": v(21.1, 21.1) * mm, "end": v(26.43, 22.83) * mm});
            skLineSegment(sketch, "E12.35.1", {"start": v(21.1, 21.1) * mm, "end": v(22.83, 26.43) * mm});
            skLineSegment(sketch, "E12.35.2", {"start": v(24.7, 24.7) * mm, "end": v(21.1, 21.1) * mm, "construction": true});
            skArc(sketch, "E12.35.3", {"start": v(26.43, 22.83) * mm, "mid": v(24.7, 24.7) * mm, "end": v(22.83, 26.43) * mm});
            skLineSegment(sketch, "E12.36.0", {"start": v(17.54, 24.15) * mm, "end": v(22.53, 26.69) * mm});
            skLineSegment(sketch, "E12.36.1", {"start": v(17.54, 24.15) * mm, "end": v(18.42, 29.67) * mm});
            skLineSegment(sketch, "E12.36.2", {"start": v(20.53, 28.25) * mm, "end": v(17.54, 24.15) * mm, "construction": true});
            skArc(sketch, "E12.36.3", {"start": v(22.53, 26.69) * mm, "mid": v(20.53, 28.25) * mm, "end": v(18.42, 29.67) * mm});
            skLineSegment(sketch, "E12.37.0", {"start": v(13.55, 26.6) * mm, "end": v(18.08, 29.88) * mm});
            skLineSegment(sketch, "E12.37.1", {"start": v(13.55, 26.6) * mm, "end": v(13.55, 32.19) * mm});
            skLineSegment(sketch, "E12.37.2", {"start": v(15.86, 31.12) * mm, "end": v(13.55, 26.6) * mm, "construction": true});
            skArc(sketch, "E12.37.3", {"start": v(18.08, 29.88) * mm, "mid": v(15.86, 31.12) * mm, "end": v(13.55, 32.19) * mm});
            skLineSegment(sketch, "E12.38.0", {"start": v(9.22, 28.38) * mm, "end": v(13.18, 32.34) * mm});
            skLineSegment(sketch, "E12.38.1", {"start": v(9.22, 28.38) * mm, "end": v(8.35, 33.91) * mm});
            skLineSegment(sketch, "E12.38.2", {"start": v(10.8, 33.22) * mm, "end": v(9.22, 28.38) * mm, "construction": true});
            skArc(sketch, "E12.38.3", {"start": v(13.18, 32.34) * mm, "mid": v(10.8, 33.22) * mm, "end": v(8.35, 33.91) * mm});
            skLineSegment(sketch, "E12.39.0", {"start": v(4.67, 29.48) * mm, "end": v(7.96, 34) * mm});
            skLineSegment(sketch, "E12.39.1", {"start": v(4.67, 29.48) * mm, "end": v(2.94, 34.8) * mm});
            skLineSegment(sketch, "E12.39.2", {"start": v(5.46, 34.5) * mm, "end": v(4.67, 29.48) * mm, "construction": true});
            skArc(sketch, "E12.39.3", {"start": v(7.96, 34) * mm, "mid": v(5.46, 34.5) * mm, "end": v(2.94, 34.8) * mm});
            skSolve(sketch);
        }
        {
            var Q0;
            Q0=qSketchRegion(id+"F8",true);
            extrude(context, id + "F9", {"entities" : qUnion([Q0]), "operationType" : NewBodyOperationType.REMOVE, "oppositeDirection" : true, "depth" : 25.4 * mm, "offsetDistance" : 25.4 * mm});
        }
        {
            var Q0;
            Q0=qCreatedBy(makeId("Front.planeOp"),FACE);
            var sketch = newSketch(context, id + "F10", { "sketchPlane" : qUnion([Q0])});
            skLineSegment(sketch, "E13.bottom", {"start": v(-50.8, 0) * mm, "end": v(50.8, 0) * mm});
            skLineSegment(sketch, "E13.left", {"start": v(-50.8, 0) * mm, "end": v(-50.8, 25.4) * mm});
            skLineSegment(sketch, "E13.right", {"start": v(50.8, 0) * mm, "end": v(50.8, 25.4) * mm});
            skLineSegment(sketch, "E14", {"start": v(-50.8, 25.4) * mm, "end": v(50.8, 25.4) * mm});
            skSolve(sketch);
        }
        {
            var Q0;
            Q0 = qSketchRegion(id + "F10", true);
            extrude(context, id + "F11", {"entities" : qUnion([Q0]), "operationType" : NewBodyOperationType.REMOVE, "endBound" : BoundingType.THROUGH_ALL, "oppositeDirection" : true, "depth" : 25.4 * mm, "offsetDistance" : 25.4 * mm, "hasSecondDirection" : true, "secondDirectionBound" : BoundingType.THROUGH_ALL, "secondDirectionOppositeDirection" : false, "secondDirectionDepth" : 25.4 * mm});
        }
        {
            var Q0;
            Q0=makeQuery(id+"F5.opExtrude","CAP_FACE",FACE,{"disambiguationData":[OSD([sQuery(id+"F4.wireOp",EDGE,"E2")])],"isStart":false});
            var sketch = newSketch(context, id + "F12", { "sketchPlane" : qUnion([Q0])});
            skCircle(sketch, "E15", {"center": v(-13.21, 11.86) * mm, "radius": 5.18 * mm});
            skSolve(sketch);
        }
        {
            var Q0;
            Q0=makeQuery(id+"F12.imprint","IMPRINT",FACE,{"disambiguationData":[TD([[makeQuery(id+"F12.imprint","IMPRINT",EDGE,{"derivedFrom":sQuery(id+"F12.wireOp",EDGE,"E15")}),1.0]])]});
            extrude(context, id + "F13", {"entities" : qUnion([Q0]), "operationType" : NewBodyOperationType.REMOVE, "oppositeDirection" : true, "depth" : 25.4 * mm, "offsetDistance" : 25.4 * mm});
        }
    });
